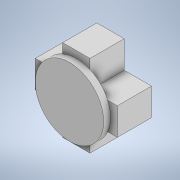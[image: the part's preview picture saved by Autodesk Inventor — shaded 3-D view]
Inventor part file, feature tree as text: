
AUTODESK INVENTOR PART (.ipt)
format: ipt  version: 2020.1 (Build 241239000, 239)  size: 127,488 bytes
history: native  units: mm
features: extrude x2, sketch x2
ambient origin geometry x8: Origin, YZ Plane, XZ Plane, XY Plane, X Axis, Y Axis, Z Axis, Center Point
bodies: Solid1 (feature_tree)
feature tree (4):
  extrude  "Extrusion1"  Depth=2.0mm
  extrude  "Extrusion2"  Depth=1.0mm
  sketch  "Sketch1"  dims[d2=2.0mm d3=2.0mm]
  sketch  "Sketch2"  dims[d4=2.0mm d5=2.0mm d6=2.0mm d7=2.0mm d8=2.0mm d9=2.0mm d10=5.0mm d11=0.0mm d12=10.0mm d13=1.0mm d14=0.0mm]
